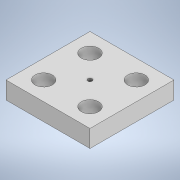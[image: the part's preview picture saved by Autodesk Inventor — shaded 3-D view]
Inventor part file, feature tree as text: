
AUTODESK INVENTOR PART (.ipt)
format: ipt  version: 2020 (Build 240168000, 168)  size: 209,408 bytes
history: native  units: mm
features: sketch x4, extrude x3, fillet x3, hole x1
ambient origin geometry x8: Origin, YZ Plane, XZ Plane, XY Plane, X Axis, Y Axis, Z Axis, Center Point
bodies: Solid1 (feature_tree)
feature tree (11):
  extrude  "Extrusion1"  Depth=4.5mm
  extrude  "Extrusion2"  Depth=4.5mm
  extrude  "Extrusion3"  Depth=2.5mm
  hole  "Hole1"  [1 undecoded]
  fillet  "Fillet1"  Radius=2.5mm
  fillet  "Fillet2"  Radius=2.5mm
  fillet  "Fillet3"  Radius=5.0mm
  sketch  "Sketch2"  dims[d12=4.5mm d13=4.5mm]
  sketch  "Sketch3"  dims[d14=4.5mm d15=4.5mm]
  sketch  "Sketch4"  dims[d16=4.5mm d17=2.5mm]
  sketch  "Sketch5"  dims[d18=2.5mm d19=2.5mm d20=2.5mm d21=2.5mm d22=5.0mm d23=0.5mm d24=0.0mm d25=25.0mm d26=25.0mm d27=6.0mm d28=6.0mm d29=6.0mm d30=6.0mm d31=1.5mm d32=5.0mm d33=0.0mm d34=14.5mm d35=14.5mm d36=14.5mm d37=14.5mm d38=14.5mm d39=14.5mm d40=1.0mm d41=5.0mm d42=0.0mm d43=0.0mm d45=2.0mm d46=2.0mm d47=6.0mm d48=4.0mm d49=2.0mm d50=90.0deg d51=2.0mm d52=0.0mm d53=1.0mm d54=1.0mm d55=0.15mm d56=0.375mm]
note: 1 required parameter value undecoded (feature->parameter linkage not recoverable at this tier; creation-order binding heuristic only, values carry confidence <= 0.55)
